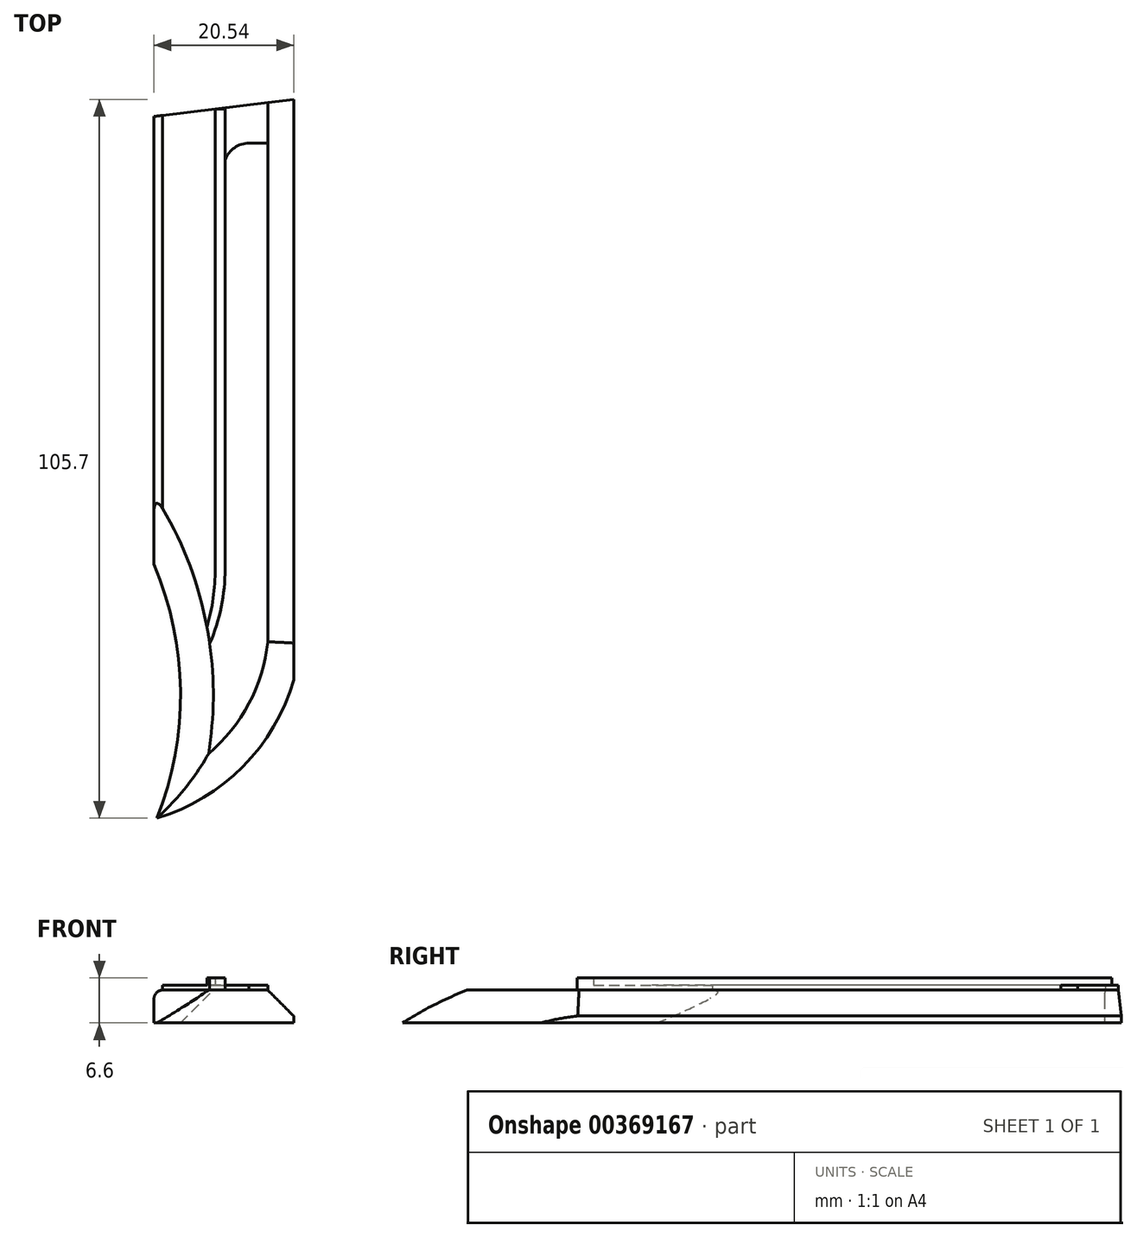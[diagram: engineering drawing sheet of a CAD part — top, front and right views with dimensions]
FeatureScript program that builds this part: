
annotation { "Feature Type Name" : "Feature", "Feature Type Description" : "" }
export const myFeature = defineFeature(function(context is Context, id is Id, definition is map)
    precondition{}
    {
        {
            var Q0;
            Q0=qCreatedBy(makeId("Top.planeOp"),FACE);
            var sketch = newSketch(context, id + "F0", { "sketchPlane" : qUnion([Q0])});
            skArc(sketch, "E0", {"start": v(0, -37.07) * mm, "mid": v(3.64, -18.53) * mm, "end": v(0, 0) * mm});
            skLineSegment(sketch, "E1", {"start": v(0, 66.51) * mm, "end": v(0, 0) * mm});
            skArc(sketch, "E2", {"start": v(0, -37.07) * mm, "mid": v(14.95, -27.4) * mm, "end": v(21.8, -10.98) * mm});
            skLineSegment(sketch, "E3", {"start": v(21.8, -10.98) * mm, "end": v(21.8, 69.17) * mm});
            skLineSegment(sketch, "E4", {"start": v(21.8, 69.17) * mm, "end": v(0, 66.51) * mm});
            skSolve(sketch);
        }
        {
            var Q0;
            Q0=makeQuery(id+"F0.imprint","IMPRINT",FACE,{"disambiguationData":[TD([[makeQuery(id+"F0.imprint","IMPRINT",EDGE,{"derivedFrom":sQuery(id+"F0.wireOp",EDGE,"E0")}),-1.0]])]});
            extrude(context, id + "F1", {"entities" : qUnion([Q0]), "depth" : 4.83 * mm});
        }
        {
            var Q0;
            Q0=makeQuery(id+"F1.opExtrude","CAP_EDGE",EDGE,{"disambiguationData":[OSD([sQuery(id+"F0.wireOp",EDGE,"E0")])],"isStart":false});
            chamfer(context, id + "F2", {"entities" : qUnion([Q0]), "width" : 5.08 * mm, "tangentPropagation" : true});
        }
        {
            var Q0;
            Q0=makeQuery(id+"F1.opExtrude","CAP_EDGE",EDGE,{"disambiguationData":[OSD([sQuery(id+"F0.wireOp",EDGE,"E2")])],"isStart":false});
            var Q1;
            Q1=makeQuery(id+"F1.opExtrude","CAP_EDGE",EDGE,{"disambiguationData":[OSD([sQuery(id+"F0.wireOp",EDGE,"E3")])],"isStart":false});
            chamfer(context, id + "F3", {"entities" : qUnion([Q0, Q1]), "width" : 5.08 * mm, "tangentPropagation" : true});
        }
        {
            var Q0;
            Q0=makeQuery(id+"F3.opChamfer","BLEND_FACE",FACE,{"disambiguationData":[OSD([sQuery(id+"F0.wireOp",EDGE,"E3")])]});
            var sketch = newSketch(context, id + "F4", { "sketchPlane" : qUnion([Q0])});
            skLineSegment(sketch, "E5", {"start": v(-10.92, -13.86) * mm, "end": v(68.85, -13.86) * mm});
            skPoint(sketch, "E5.endSnap0", {"position": v(68.85, -11.83) * mm});
            skSolve(sketch);
        }
        {
            var Q0;
            {var subQ0=sQuery(id+"F0.wireOp",EDGE,"E3");Q0=makeQuery(id+"F3.opChamfer","BLEND_EDGE",EDGE,{"blendedFrom":[makeQuery(id+"F1.opExtrude","CAP_EDGE",EDGE,{"disambiguationData":[OSD([subQ0])],"isStart":false}),makeQuery(id+"F1.opExtrude","CAP_FACE",FACE,{"disambiguationData":[OSD([sQuery(id+"F0.wireOp",EDGE,"E0"),sQuery(id+"F0.wireOp",EDGE,"E1"),sQuery(id+"F0.wireOp",EDGE,"E2"),subQ0,sQuery(id+"F0.wireOp",EDGE,"E4")])],"isStart":true})],"blendedInto":[makeQuery(id+"F1.opExtrude","CAP_FACE",FACE,{"disambiguationData":[OSD([sQuery(id+"F0.wireOp",EDGE,"E0"),sQuery(id+"F0.wireOp",EDGE,"E1"),sQuery(id+"F0.wireOp",EDGE,"E2"),subQ0,sQuery(id+"F0.wireOp",EDGE,"E4")])],"isStart":true})]});}
            chamfer(context, id + "F5", {"entities" : qUnion([Q0]), "chamferType" : ChamferType.OFFSET_ANGLE, "width" : 1.02 * mm, "oppositeDirection" : false, "angle" : 90 * degree, "tangentPropagation" : true});
        }
        {
            var Q0;
            Q0=makeQuery(id+"F1.opExtrude","CAP_EDGE",EDGE,{"disambiguationData":[OSD([sQuery(id+"F0.wireOp",EDGE,"E1")])],"isStart":false});
            fillet(context, id + "F6", {"entities" : qUnion([Q0]), "radius" : 1.27 * mm, "tangentPropagation" : true, "allowEdgeOverflow" : false});
        }
        {
            var Q0;
            Q0=makeQuery(id+"F1.opExtrude","CAP_FACE",FACE,{"disambiguationData":[OSD([sQuery(id+"F0.wireOp",EDGE,"E0"),sQuery(id+"F0.wireOp",EDGE,"E1"),sQuery(id+"F0.wireOp",EDGE,"E2"),sQuery(id+"F0.wireOp",EDGE,"E3"),sQuery(id+"F0.wireOp",EDGE,"E4")])],"isStart":false});
            var sketch = newSketch(context, id + "F7", { "sketchPlane" : qUnion([Q0])});
            skLineSegment(sketch, "E6.bottom", {"start": v(9, 67.61) * mm, "end": v(10.46, 67.61) * mm});
            skLineSegment(sketch, "E6.top", {"start": v(9, 0) * mm, "end": v(10.46, 0) * mm});
            skLineSegment(sketch, "E6.left", {"start": v(9, 67.61) * mm, "end": v(9, 0) * mm});
            skLineSegment(sketch, "E6.right", {"start": v(10.46, 67.61) * mm, "end": v(10.46, 0) * mm});
            skArc(sketch, "E7", {"start": v(7.8, -8.58) * mm, "mid": v(8.7, -4.33) * mm, "end": v(9, 0) * mm});
            skArc(sketch, "E8", {"start": v(8.2, -11) * mm, "mid": v(9.89, -5.62) * mm, "end": v(10.46, 0) * mm});
            skArc(sketch, "E9", {"start": v(13.98, 62.57) * mm, "mid": v(11.83, 61.92) * mm, "end": v(10.46, 60.14) * mm});
            skLineSegment(sketch, "E10", {"start": v(13.98, 62.57) * mm, "end": v(16.73, 62.57) * mm});
            skSolve(sketch);
        }
        {
            var Q0;
            Q0=makeQuery(id+"F7.imprint","IMPRINT",FACE,{"disambiguationData":[TD([[makeQuery(id+"F7.imprint","IMPRINT",EDGE,{"derivedFrom":sQuery(id+"F7.wireOp",EDGE,"E6.top")}),-1.0]])]});
            var Q1;
            Q1=makeQuery(id+"F7.imprint","IMPRINT",FACE,{"disambiguationData":[TD([[makeQuery(id+"F7.imprint","IMPRINT",EDGE,{"derivedFrom":sQuery(id+"F7.wireOp",EDGE,"E6.bottom")}),-1.0]])]});
            extrude(context, id + "F8", {"entities" : qUnion([Q0, Q1]), "operationType" : NewBodyOperationType.ADD, "depth" : 1.78 * mm});
        }
        {
            var Q0;
            {var subQ3=sQuery(id+"F7.wireOp",EDGE,"E6.bottom");Q0=makeQuery(id+"F7.imprint","IMPRINT",FACE,{"disambiguationData":[TD([[makeQuery(id+"F7.imprint","IMPRINT",EDGE,{"derivedFrom":subQ3}),1.0]])]});}
            var Q1;
            {var subQ7=sQuery(id+"F7.wireOp",EDGE,"E6.left");Q1=makeQuery(id+"F7.imprint","IMPRINT",FACE,{"disambiguationData":[TD([[makeQuery(id+"F7.imprint","IMPRINT",EDGE,{"derivedFrom":subQ7}),-1.0]])]});}
            extrude(context, id + "F9", {"entities" : qUnion([Q0, Q1]), "operationType" : NewBodyOperationType.ADD, "depth" : 0.71 * mm});
        }
    });
